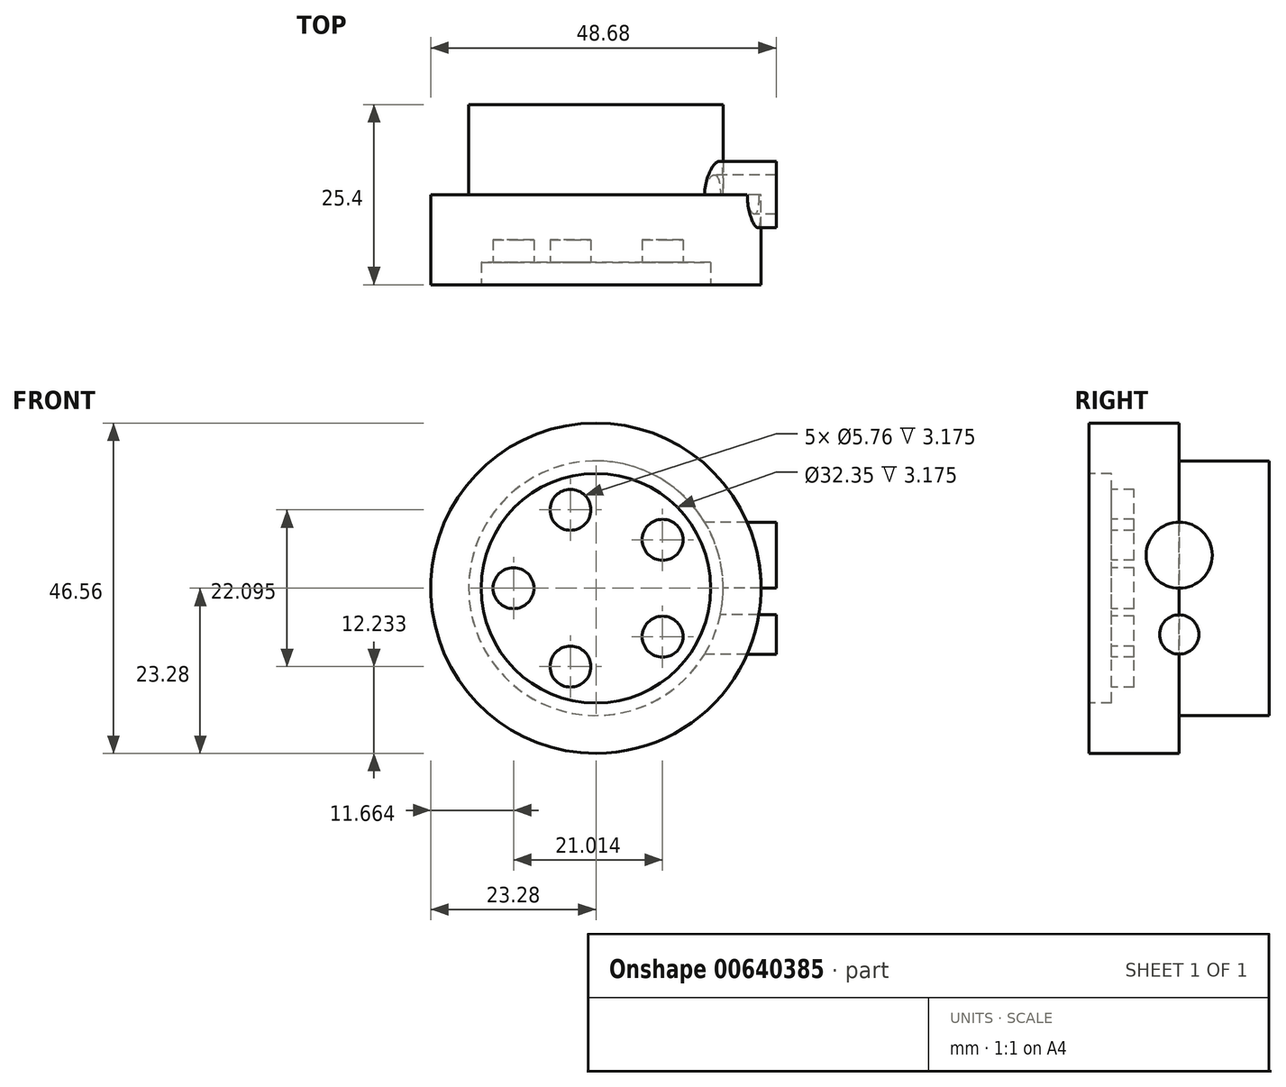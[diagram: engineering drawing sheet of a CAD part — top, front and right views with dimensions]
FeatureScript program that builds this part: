
annotation { "Feature Type Name" : "Feature", "Feature Type Description" : "" }
export const myFeature = defineFeature(function(context is Context, id is Id, definition is map)
    precondition{}
    {
        {
            var Q0;
            Q0=qCreatedBy(makeId("Front.planeOp"),FACE);
            var sketch = newSketch(context, id + "F0", { "sketchPlane" : qUnion([Q0])});
            skCircle(sketch, "E0", {"center": v(0, 0) * mm, "radius": 23.28 * mm});
            skSolve(sketch);
        }
        {
            var Q0;
            Q0 = qSketchRegion(id + "F0", true);
            extrude(context, id + "F1", {"entities" : qUnion([Q0]), "depth" : 12.7 * mm, "offsetDistance" : 25.4 * mm});
        }
        {
            var Q0;
            Q0=makeQuery(id+"F1.opExtrude","CAP_FACE",FACE,{"disambiguationData":[OSD([sQuery(id+"F0.wireOp",EDGE,"E0")])],"isStart":false});
            var sketch = newSketch(context, id + "F2", { "sketchPlane" : qUnion([Q0])});
            skCircle(sketch, "E1", {"center": v(0, 0) * mm, "radius": 16.17 * mm});
            skSolve(sketch);
        }
        {
            var Q0;
            Q0 = qSketchRegion(id + "F2", true);
            extrude(context, id + "F3", {"entities" : qUnion([Q0]), "operationType" : NewBodyOperationType.REMOVE, "oppositeDirection" : true, "depth" : 3.17 * mm, "offsetDistance" : 25.4 * mm});
        }
        {
            var Q0;
            Q0=makeQuery(id+"F1.opExtrude","CAP_FACE",FACE,{"disambiguationData":[OSD([sQuery(id+"F0.wireOp",EDGE,"E0")])],"isStart":true});
            var sketch = newSketch(context, id + "F4", { "sketchPlane" : qUnion([Q0])});
            skCircle(sketch, "E2", {"center": v(0, 0) * mm, "radius": 17.94 * mm});
            skSolve(sketch);
        }
        {
            var Q0;
            Q0 = qSketchRegion(id + "F4", true);
            extrude(context, id + "F5", {"entities" : qUnion([Q0]), "operationType" : NewBodyOperationType.ADD, "depth" : 12.7 * mm, "offsetDistance" : 25.4 * mm});
        }
        {
            var Q0;
            Q0=makeQuery(id+"F3.boolean.opBoolean","COPY",FACE,{"derivedFrom":makeQuery(id+"F3.opExtrude","CAP_FACE",FACE,{"disambiguationData":[OSD([sQuery(id+"F2.wireOp",EDGE,"E1")])],"isStart":false})});
            var sketch = newSketch(context, id + "F6", { "sketchPlane" : qUnion([Q0])});
            skCircle(sketch, "E3", {"center": v(0, 0) * mm, "radius": 11.62 * mm, "construction": true});
            skCircle(sketch, "E4", {"center": v(-11.62, 0) * mm, "radius": 2.88 * mm});
            skCircle(sketch, "E5.1.0", {"center": v(-3.59, -11.05) * mm, "radius": 2.88 * mm});
            skCircle(sketch, "E5.2.0", {"center": v(9.4, -6.83) * mm, "radius": 2.88 * mm});
            skCircle(sketch, "E5.3.0", {"center": v(9.4, 6.83) * mm, "radius": 2.88 * mm});
            skCircle(sketch, "E5.4.0", {"center": v(-3.59, 11.05) * mm, "radius": 2.88 * mm});
            skSolve(sketch);
        }
        {
            var Q0;
            Q0 = qSketchRegion(id + "F6", true);
            extrude(context, id + "F7", {"entities" : qUnion([Q0]), "operationType" : NewBodyOperationType.REMOVE, "oppositeDirection" : true, "depth" : 3.17 * mm, "offsetDistance" : 25.4 * mm});
        }
        {
            var Q0;
            Q0=qCreatedBy(makeId("Right.planeOp"),FACE);
            var sketch = newSketch(context, id + "F8", { "sketchPlane" : qUnion([Q0])});
            skCircle(sketch, "E6", {"center": v(0, 4.66) * mm, "radius": 4.66 * mm});
            skSolve(sketch);
        }
        {
            var Q0;
            Q0 = qSketchRegion(id + "F8", true);
            extrude(context, id + "F9", {"entities" : qUnion([Q0]), "operationType" : NewBodyOperationType.ADD, "depth" : 25.4 * mm, "offsetDistance" : 25.4 * mm});
        }
        {
            var Q0;
            Q0=qCreatedBy(makeId("Right.planeOp"),FACE);
            var sketch = newSketch(context, id + "F10", { "sketchPlane" : qUnion([Q0])});
            skCircle(sketch, "E7", {"center": v(0, -6.52) * mm, "radius": 2.77 * mm});
            skSolve(sketch);
        }
        {
            var Q0;
            Q0 = qSketchRegion(id + "F10", true);
            extrude(context, id + "F11", {"entities" : qUnion([Q0]), "operationType" : NewBodyOperationType.ADD, "depth" : 25.4 * mm, "offsetDistance" : 25.4 * mm});
        }
    });
